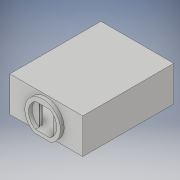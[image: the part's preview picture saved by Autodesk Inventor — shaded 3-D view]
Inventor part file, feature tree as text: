
AUTODESK INVENTOR PART (.ipt)
format: ipt  version: 2017 (Build 210142000, 142)  size: 177,664 bytes
history: native  units: in
note: dims shown in document units (in); Inventor stores cm internally (conversion verified against a paired STEP export)
features: extrude x6, sketch x6, mirror x2
ambient origin geometry x8: Origin, YZ Plane, XZ Plane, XY Plane, X Axis, Y Axis, Z Axis, Center Point
bodies: Solid1 (feature_tree)
feature tree (14):
  extrude  "floor"  Depth=25.0in
  extrude  "walls"  Depth=1.0in
  extrude  "doorframe"  Depth=1.0in
  extrude  "ceiling"  Depth=8.6667in TaperAngle=0.0deg
  extrude  "left door slot"  Depth=6.6667in
  mirror  "mirror door slot"
  mirror  "right door slot"
  extrude  "corridor connect"  Depth=1.0in TaperAngle=0.0deg
  sketch  "Sketch1"  dims[d0=20.0in d1=25.0in]
  sketch  "Sketch4"  dims[d2=1.0in d3=0.0in d11=1.0in]
  sketch  "Sketch5"  dims[d12=1.0in d13=1.0in]
  sketch  "Sketch7"  dims[d14=1.0in d15=8.6667in d16=0.0in]
  sketch  "Sketch8"  dims[d17=2.0in d18=6.6667in]
  sketch  "Sketch10"  dims[d20=8.6667in d21=0.0in d22=1.0in d23=0.0in d24=0.25in d25=0.5in d26=2.0in d27=0.0in d28=6.6667in d37=6.6667in d38=4.0in d39=1.0in d40=1.0in d41=0.0in]
